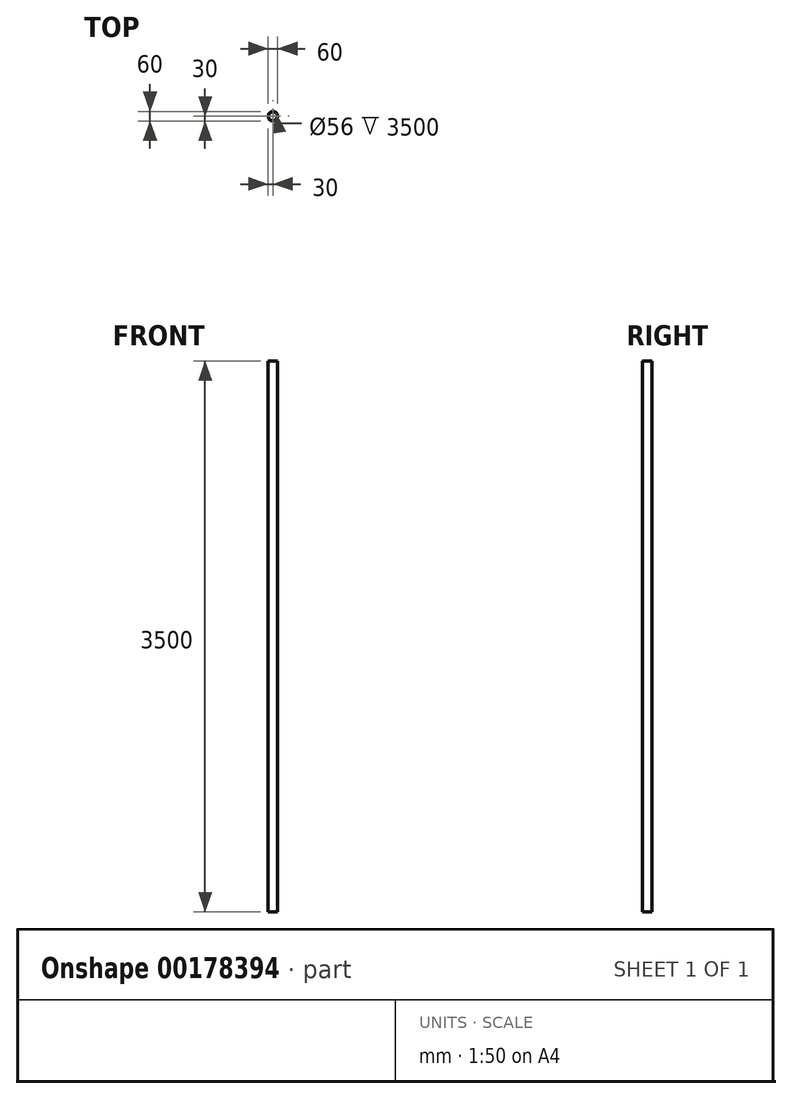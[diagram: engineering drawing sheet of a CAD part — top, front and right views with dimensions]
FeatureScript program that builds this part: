
annotation { "Feature Type Name" : "Feature", "Feature Type Description" : "" }
export const myFeature = defineFeature(function(context is Context, id is Id, definition is map)
    precondition{}
    {
        {
            var Q0;
            Q0=qCreatedBy(makeId("Top.planeOp"),FACE);
            var sketch = newSketch(context, id + "F0", { "sketchPlane" : qUnion([Q0])});
            skCircle(sketch, "E0", {"center": v(0, 0) * mm, "radius": 30 * mm});
            skCircle(sketch, "E1.0", {"center": v(0, 0) * mm, "radius": 28 * mm});
            skSolve(sketch);
        }
        {
            var Q0;
            Q0=makeQuery(id+"F0.imprint","IMPRINT",FACE,{"disambiguationData":[TD([[makeQuery(id+"F0.imprint","IMPRINT",EDGE,{"derivedFrom":sQuery(id+"F0.wireOp",EDGE,"E0")}),1.0]])]});
            extrude(context, id + "F1", {"entities" : qUnion([Q0]), "depth" : 3500 * mm});
        }
    });
